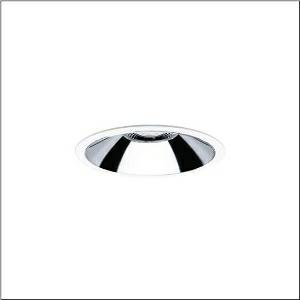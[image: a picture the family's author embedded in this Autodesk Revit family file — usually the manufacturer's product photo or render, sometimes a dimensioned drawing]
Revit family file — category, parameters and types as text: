
# Revit family: lunis_21_xl_51db15mf3d
name_source: partatom
category: Lighting Fixtures
units: mm (PartAtom-declared; Revit-internal decimal feet)

## family parameters
Cut with Voids When Loaded = No
Host = Face
Light Source = No
Part Type = Normal
Room Calculation Point = No
Round Connector Dimension = Use Diameter
Shared = No

## types (1)
- --- (1 x LED, 2620 lm, 23.5 W, 3000K)
    Apparent Load = 24 VA
    CIE Flux Codes = 89 99 100 100 100
    Color Rendering = 80
    Color Temperature = 3000K
    Default Elevation = 1800 mm
    Description = Lunis 21,  XL, downlight, of PC, light emission: direct distribution, LED rated luminous flux: 2.180lm, light colour: 830, control gear: ECG, with terminal, 3-pole, mains connection: 220..240V, AC, housing, round, of diecast aluminium, traffic white (RAL 9016), diameter: 213mm, protection rating (complete): IP20, insulation class (complete): insulation class II (safety insulation), certification: CE, impact resistance: IK02, packaging unit: 1 piece
    Height = 0 mm  [stored 0 ft]
    Lamp = 1 x LED
    Lamp Light Flux = 2620 lm
    Lamp Power = 23.5 W
    Lamp count = 1
    Length = 213 mm
    Luminous efficacy = 111 lm/W
    Manufacturer = Siteco
    ModVariant = No
    Model = 51DB15MF3D
    Mounting Place = Ceiling
    Mounting Type = Recessed
    Number of Poles = 1
    OnlyDefault = Yes
    Power Factor = 1
    Product Name = Lunis 21 XL
    Product group = downlight | ceiling recessed
    ProductGroupID = 402
    Protection Class = Protection class II
    Protection Degree = IP 20
    RLX_Detail_Level = 1
    RlxData = <blob elided: 27601 chars, md5=a3a1408b>
    Socket = socket
    Standby Power = 0 W
    System Light Flux = 2620 lm
    System Power = 24 W
    Type Comments = factory setting: luminous flux: 100 % | (ON | ON)
    Type Image = l_1006990.jpg
    URL = http://relux.com
    VarID = @adj_060597
    Voltage = 0 V
    Weight = 0.00 kg
    Width = 0 mm  [stored 0 ft]

note: [stored X ft] marks values corroborated as IEEE doubles in the binary element streams (Revit-internal decimal feet)

## geometry (parser evidence)
native form markers: Blend x4, Sweep x11
no freeform markers — native parametric forms only
